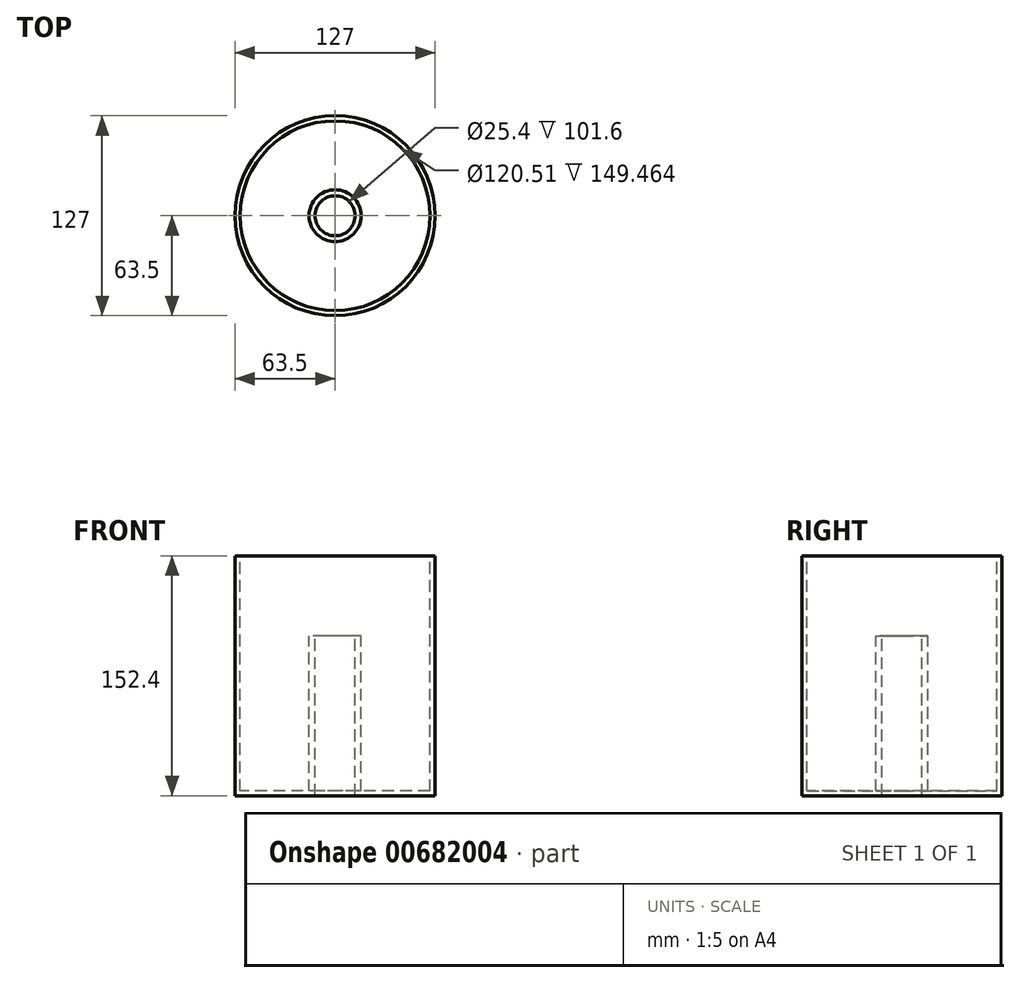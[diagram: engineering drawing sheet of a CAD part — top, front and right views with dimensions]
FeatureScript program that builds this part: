
annotation { "Feature Type Name" : "Feature", "Feature Type Description" : "" }
export const myFeature = defineFeature(function(context is Context, id is Id, definition is map)
    precondition{}
    {
        {
            var Q0;
            Q0=qCreatedBy(makeId("Front.planeOp"),FACE);
            var sketch = newSketch(context, id + "F0", { "sketchPlane" : qUnion([Q0])});
            skLineSegment(sketch, "E0", {"start": v(0, 101.6) * mm, "end": v(0, -25.4) * mm});
            skLineSegment(sketch, "E1", {"start": v(0, 101.6) * mm, "end": v(12.7, 101.6) * mm});
            skLineSegment(sketch, "E2", {"start": v(12.7, 101.6) * mm, "end": v(12.7, 0) * mm});
            skLineSegment(sketch, "E3", {"start": v(12.7, 0) * mm, "end": v(38.1, 0) * mm});
            skLineSegment(sketch, "E4", {"start": v(12.7, 101.6) * mm, "end": v(16.51, 101.6) * mm});
            skLineSegment(sketch, "E5", {"start": v(16.51, 101.6) * mm, "end": v(16.51, 6.35) * mm});
            skLineSegment(sketch, "E6", {"start": v(38.1, 0) * mm, "end": v(63.5, 0) * mm});
            skLineSegment(sketch, "E7", {"start": v(63.5, 0) * mm, "end": v(63.5, 152.4) * mm});
            skLineSegment(sketch, "E8", {"start": v(16.51, 6.35) * mm, "end": v(16.51, 2.94) * mm});
            skLineSegment(sketch, "E9", {"start": v(16.51, 2.94) * mm, "end": v(60.26, 2.94) * mm});
            skLineSegment(sketch, "E10", {"start": v(60.26, 2.94) * mm, "end": v(60.26, 152.4) * mm});
            skLineSegment(sketch, "E11", {"start": v(60.26, 152.4) * mm, "end": v(63.5, 152.4) * mm});
            skSolve(sketch);
        }
        {
            var Q0;
            Q0=makeQuery(id+"F0.imprint","IMPRINT",FACE,{"disambiguationData":[TD([[makeQuery(id+"F0.imprint","IMPRINT",EDGE,{"derivedFrom":sQuery(id+"F0.wireOp",EDGE,"E2")}),1.0]])]});
            var Q1;
            Q1=sQuery(id+"F0.wireOp",EDGE,"E0");
            revolve(context, id + "F1", {"entities" : qUnion([Q0]), "axis" : qUnion([Q1]), "revolveType" : RevolveType.FULL});
        }
    });
